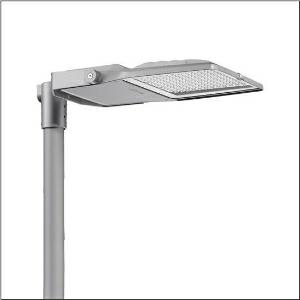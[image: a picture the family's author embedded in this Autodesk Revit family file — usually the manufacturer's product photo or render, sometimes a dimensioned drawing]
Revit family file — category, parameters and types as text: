
# Revit family: floodlight_fl_21_iq_midi___pl61_5xa7782f4c3a_0871
name_source: partatom
category: Lighting Fixtures
units: mm (PartAtom-declared; Revit-internal decimal feet)

## family parameters
Cut with Voids When Loaded = No
Host = Face
Light Source = No
Part Type = Normal
Room Calculation Point = No
Round Connector Dimension = Use Diameter
Shared = No

## types (1)
- --- (1 x LED, 36650 lm, 270.2 W, 4000K)
    Apparent Load = 270 VA
    CIE Flux Codes = 33 65 98 100 100
    Color Rendering = 70
    Color Temperature = 4000K
    Default Elevation = 1800 mm
    Description = Floodlight FL 21 iQ midi, floodlight, primary light control with lens, of PMMA, primary optical cover: protective disc, of toughened safety glass, transparent, light distribution: PL61, light emission: direct distribution, installation type: surface-mounted, lamps: LED, High Power LED, rated values: 36.650lm | 270,2W | 135,6lm/W (begin service life); end service life: 36.650lm | 286,6W; at 50% lumin. flux: 18.325lm | 117,7W | 155,7lm/W, colour temperature: 4000K, colour rendering: CRI > 70, light colour: 740, light setting 1 begin service life: 100% | 36.650lm | 270,2W | 135,6lm/W | 4.000K, light setting 1 end service life: 286,6W, further light settings possible, control: optimised constant luminous flux control (CLO 2.0), Desk-Remote (wireless, voltage-free reading and setting of iQ features in the workshop via application-optimized NFC function/RFID function), Smart-Wire, Night-Set, Temp-Guard, Auto-Match, Street-Remote, pre-setting: linear dimming characteristic, with terminal, 6-pole, mains connection: 220..240V, AC, 50/60Hz, luminaire housing, of diecast aluminium, powder-coated, SITECO metallic grey (DB 702S), corrosivity category C5 mid according to DIN EN ISO 12944suitable for swimming poolschlorine-resistant, sealing non-destructively replaceable, please order mast flange separately, mast bracket, of steel, galvanised, powder-coated, SITECO metallic grey (DB 702S), protection rating (complete): IP66, insulation class (complete): insulation class II (safety insulation), certification: CE, ENEC, VDE, protection symbol: D, impact resistance: IK08, permissible operating ambient temperature: -40..+40°C, permissible operating ambient temperature for outdoor applications: -40..+50°C, standard: DIN EN 12944, LABS conformity tested according to VDMA 24364:2018-05, packaging unit: 1 piece

Light Distribution: PL61
    Height = 76 mm
    Lamp = 1 x LED
    Lamp Light Flux = 36650 lm
    Lamp Power = 270.2 W
    Lamp count = 1
    Length = 657 mm
    Luminous efficacy = 136 lm/W
    Manufacturer = Siteco
    ModVariant = No
    Model = 5XA7782F4C3A
    Number of Poles = 1
    OnlyDefault = Yes
    Power Factor = 1
    Product Name = Floodlight FL 21 iQ midi | PL61
    Product group = floodlight | pylon annexe
    ProductGroupID = 6201
    Protection Class = Protection class II
    Protection Degree = IP 66
    RLX_Detail_Level = 1
    RLX_Emergency_Light_Flux = 0 lm
    RLX_Emergency_Type = 0
    RLX_Emergency_Type_DB = No
    RlxData = <blob elided: 154009 chars, md5=3e69f181>
    Socket = socket
    Standby Power = 0 W
    System Light Flux = 36650 lm
    System Power = 270 W
    Type Comments = factory setting: luminous flux: 100 % | dim-lin: 254 | 620 mA
    Type Image = l_1007123.jpg
    URL = http://relux.com
    VarID = @adj_108129
    Voltage = 0 V
    Weight = 0.00 kg
    Width = 442 mm

## geometry (parser evidence)
native form markers: Blend x4, Sweep x11
no freeform markers — native parametric forms only
